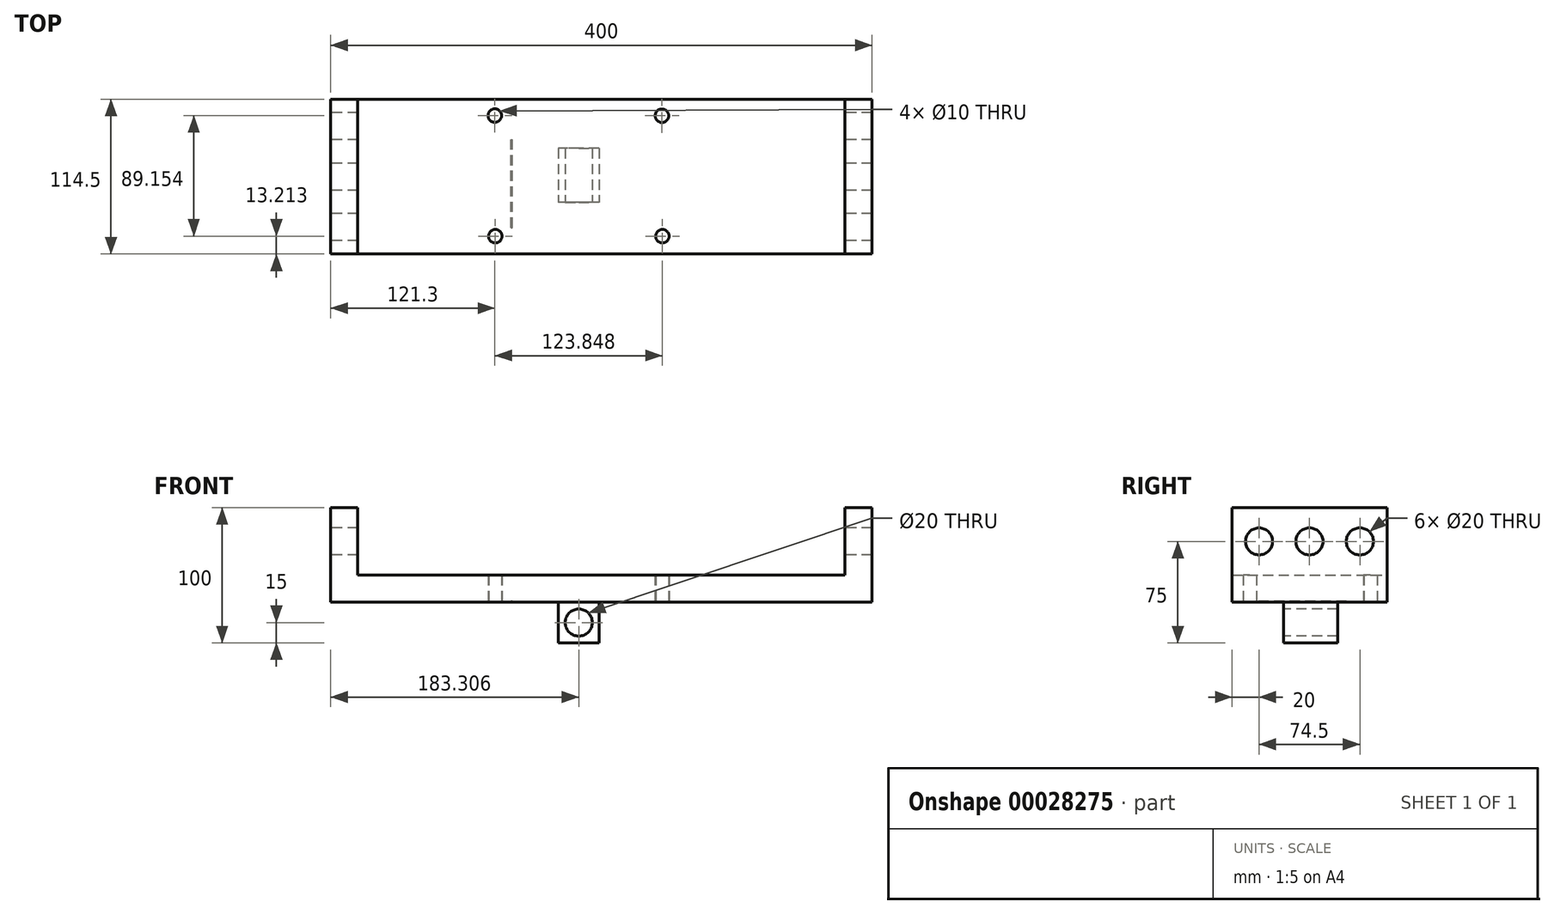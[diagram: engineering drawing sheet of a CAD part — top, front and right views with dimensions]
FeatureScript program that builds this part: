
annotation { "Feature Type Name" : "Feature", "Feature Type Description" : "" }
export const myFeature = defineFeature(function(context is Context, id is Id, definition is map)
    precondition{}
    {
        {
            var Q0;
            Q0=qCreatedBy(makeId("Top.planeOp"),FACE);
            var sketch = newSketch(context, id + "F0", { "sketchPlane" : qUnion([Q0])});
            skLineSegment(sketch, "E0.bottom", {"start": v(0, 0) * mm, "end": v(400, 0) * mm});
            skLineSegment(sketch, "E0.top", {"start": v(0, 114.5) * mm, "end": v(400, 114.5) * mm});
            skLineSegment(sketch, "E0.left", {"start": v(0, 0) * mm, "end": v(0, 114.5) * mm});
            skLineSegment(sketch, "E0.right", {"start": v(400, 0) * mm, "end": v(400, 114.5) * mm});
            skSolve(sketch);
        }
        {
            var Q0;
            Q0=makeQuery(id+"F0.imprint","IMPRINT",FACE,{"disambiguationData":[TD([[makeQuery(id+"F0.imprint","IMPRINT",EDGE,{"derivedFrom":sQuery(id+"F0.wireOp",EDGE,"E0.bottom")}),1.0]])]});
            extrude(context, id + "F1", {"entities" : qUnion([Q0]), "depth" : 20 * mm});
        }
        {
            var Q0;
            Q0=makeQuery(id+"F1.opExtrude","CAP_FACE",FACE,{"disambiguationData":[OSD([sQuery(id+"F0.wireOp",EDGE,"E0.bottom"),sQuery(id+"F0.wireOp",EDGE,"E0.top"),sQuery(id+"F0.wireOp",EDGE,"E0.left"),sQuery(id+"F0.wireOp",EDGE,"E0.right")])],"isStart":false});
            var sketch = newSketch(context, id + "F12", { "sketchPlane" : qUnion([Q0])});
            skLineSegment(sketch, "E1.bottom", {"start": v(0, 0) * mm, "end": v(20, 0) * mm});
            skLineSegment(sketch, "E1.top", {"start": v(0, 114.5) * mm, "end": v(20, 114.5) * mm});
            skLineSegment(sketch, "E1.left", {"start": v(0, 0) * mm, "end": v(0, 114.5) * mm});
            skLineSegment(sketch, "E1.right", {"start": v(20, 0) * mm, "end": v(20, 114.5) * mm});
            skLineSegment(sketch, "E2.bottom", {"start": v(400, 0) * mm, "end": v(380, 0) * mm});
            skLineSegment(sketch, "E2.top", {"start": v(400, 114.5) * mm, "end": v(380, 114.5) * mm});
            skLineSegment(sketch, "E2.left", {"start": v(400, 0) * mm, "end": v(400, 114.5) * mm});
            skLineSegment(sketch, "E2.right", {"start": v(380, 0) * mm, "end": v(380, 114.5) * mm});
            skSolve(sketch);
        }
        {
            var Q0;
            Q0 = qSketchRegion(id + "F12", true);
            extrude(context, id + "F13", {"entities" : qUnion([Q0]), "operationType" : NewBodyOperationType.ADD, "depth" : 50 * mm});
        }
        {
            var Q0;
            Q0=makeQuery(id+"F13.boolean.opBoolean","MERGE",FACE,{"derivedFrom":[makeQuery(id+"F1.opExtrude","SWEPT_FACE",FACE,{"disambiguationData":[OSD([sQuery(id+"F0.wireOp",EDGE,"E0.left")])]}),makeQuery(id+"F13.opExtrude","SWEPT_FACE",FACE,{"disambiguationData":[OSD([sQuery(id+"F12.wireOp",EDGE,"E1.left")])]})]});
            var sketch = newSketch(context, id + "F2", { "sketchPlane" : qUnion([Q0])});
            skLineSegment(sketch, "E3", {"start": v(-114.5, 70) * mm, "end": v(0, 70) * mm});
            skCircle(sketch, "E4", {"center": v(-20, 45) * mm, "radius": 10 * mm});
            skCircle(sketch, "E5", {"center": v(-94.5, 45) * mm, "radius": 10 * mm});
            skCircle(sketch, "E6", {"center": v(-57.25, 45) * mm, "radius": 10 * mm});
            skSolve(sketch);
        }
        {
            var Q0;
            Q0 = qSketchRegion(id + "F2", true);
            var Q1;
            {var subQ0=sQuery(id+"F2.wireOp",EDGE,"f415a451-caa5-4d60-8094-ee07f51d5886");var subQ1=sQuery(id+"F2.wireOp",EDGE,"d71bda7b-f379-47d4-bd46-1eae14bf07e1");var subQ3=makeQuery(id+"F2.imprint","INTERSECT",VERTEX,{"disambiguationData":[OD(0.0)],"derivedFrom":[subQ1,subQ0]});Q1=makeQuery(id+"F2.imprint","IMPRINT",FACE,{"disambiguationData":[TD([[makeQuery(id+"F2.imprint","IMPRINT",EDGE,{"disambiguationData":[TD([[subQ3,-1.0]])],"derivedFrom":subQ1}),1.0]])]});}
            extrude(context, id + "F3", {"entities" : qUnion([Q0, Q1]), "operationType" : NewBodyOperationType.REMOVE, "oppositeDirection" : true, "depth" : 410 * mm});
        }
        {
            var Q0;
            Q0=makeQuery(id+"F1.opExtrude","CAP_FACE",FACE,{"disambiguationData":[OSD([sQuery(id+"F0.wireOp",EDGE,"E0.bottom"),sQuery(id+"F0.wireOp",EDGE,"E0.top"),sQuery(id+"F0.wireOp",EDGE,"E0.left"),sQuery(id+"F0.wireOp",EDGE,"E0.right")])],"isStart":true});
            var sketch = newSketch(context, id + "F14", { "sketchPlane" : qUnion([Q0])});
            skCircle(sketch, "E7", {"center": v(121.3, -102.37) * mm, "radius": 5 * mm});
            skCircle(sketch, "E8", {"center": v(244.76, -102.25) * mm, "radius": 5 * mm});
            skCircle(sketch, "E9.MirrorC", {"center": v(245.15, -13.21) * mm, "radius": 5 * mm});
            skLineSegment(sketch, "E10.MirrorC", {"start": v(221.38, -13.21) * mm, "end": v(221.38, -13.21) * mm});
            skCircle(sketch, "E11.MirrorC", {"center": v(121.65, -13.21) * mm, "radius": 5 * mm});
            skPoint(sketch, "E12.orphan", {"position": v(200, -114.5) * mm});
            skPoint(sketch, "E13.end.orphan", {"position": v(200, 0) * mm});
            skPoint(sketch, "E13.start.orphan", {"position": v(200, -57.25) * mm});
            skLineSegment(sketch, "E14", {"start": v(244.76, -102.25) * mm, "end": v(121.26, -102.25) * mm});
            skLineSegment(sketch, "E15", {"start": v(245.15, -13.21) * mm, "end": v(121.65, -13.21) * mm});
            skLineSegment(sketch, "E16", {"start": v(244.76, -102.25) * mm, "end": v(245.19, -13.21) * mm});
            skLineSegment(sketch, "E17.0", {"start": v(163.78, -101.86) * mm, "end": v(164.21, -12.83) * mm});
            skSolve(sketch);
        }
        {
            var Q0;
            Q0 = qSketchRegion(id + "F14", true);
            extrude(context, id + "F4", {"entities" : qUnion([Q0]), "operationType" : NewBodyOperationType.REMOVE, "oppositeDirection" : true, "depth" : 40 * mm});
        }
        {
            var Q0;
            Q0=makeQuery(id+"F14.imprint","IMPRINT",FACE,{"disambiguationData":[TD([[makeQuery(id+"F14.imprint","IMPRINT",EDGE,{"derivedFrom":sQuery(id+"F14.wireOp",EDGE,"E7")}),-1.0]])]});
            var sketch = newSketch(context, id + "F15", { "sketchPlane" : qUnion([Q0])});
            skLineSegment(sketch, "E18.0", {"start": v(233.01, -102.2) * mm, "end": v(233.44, -13.16) * mm});
            skLineSegment(sketch, "E19.0", {"start": v(232.01, -102.19) * mm, "end": v(232.44, -13.15) * mm});
            skLineSegment(sketch, "E20", {"start": v(233.01, -102.2) * mm, "end": v(232.01, -102.19) * mm});
            skLineSegment(sketch, "E21", {"start": v(121.02, -102.28) * mm, "end": v(121.63, -13.25) * mm});
            skLineSegment(sketch, "E22", {"start": v(121.59, -19.54) * mm, "end": v(133.34, -19.62) * mm});
            skLineSegment(sketch, "E23.bottom", {"start": v(133.34, -19.62) * mm, "end": v(134.34, -19.62) * mm});
            skLineSegment(sketch, "E23.top", {"start": v(133.34, -84.48) * mm, "end": v(134.34, -84.48) * mm});
            skLineSegment(sketch, "E23.left", {"start": v(133.34, -19.62) * mm, "end": v(133.34, -84.48) * mm});
            skLineSegment(sketch, "E23.right", {"start": v(134.34, -19.62) * mm, "end": v(134.34, -84.48) * mm});
            skSolve(sketch);
        }
        {
            var Q0;
            Q0 = qSketchRegion(id + "F15", true);
            extrude(context, id + "F5", {"entities" : qUnion([Q0]), "operationType" : NewBodyOperationType.REMOVE, "oppositeDirection" : true, "depth" : 1 * mm});
        }
        {
            var Q0;
            Q0 = qSketchRegion(id + "F15", true);
            extrude(context, id + "F6", {"entities" : qUnion([Q0]), "operationType" : NewBodyOperationType.REMOVE, "oppositeDirection" : true, "depth" : 1 * mm});
        }
        {
            var Q0;
            Q0=sQuery(id+"F15.wireOp",EDGE,"E18.0");
            var Q1;
            Q1=sQuery(id+"F15.wireOp",EDGE,"E19.0");
            var Q2;
            Q2=sQuery(id+"F15.wireOp",EDGE,"E20");
            extrude(context, id + "F7", {"bodyType" : ToolBodyType.SURFACE, "surfaceEntities" : qUnion([Q0, Q1, Q2]), "oppositeDirection" : true, "depth" : 1 * mm});
        }
        {
            var Q0;
            Q0=makeQuery(id+"F1.opExtrude","CAP_FACE",FACE,{"disambiguationData":[OSD([sQuery(id+"F0.wireOp",EDGE,"E0.bottom"),sQuery(id+"F0.wireOp",EDGE,"E0.top"),sQuery(id+"F0.wireOp",EDGE,"E0.left"),sQuery(id+"F0.wireOp",EDGE,"E0.right")])],"isStart":true});
            var sketch = newSketch(context, id + "F8", { "sketchPlane" : qUnion([Q0])});
            skLineSegment(sketch, "E24.rect.bottom", {"start": v(198.3, -78.08) * mm, "end": v(168.3, -78.08) * mm});
            skLineSegment(sketch, "E24.rect.top", {"start": v(198.3, -38.08) * mm, "end": v(168.3, -38.08) * mm});
            skLineSegment(sketch, "E24.rect.left", {"start": v(198.3, -78.08) * mm, "end": v(198.3, -38.08) * mm});
            skLineSegment(sketch, "E24.rect.right", {"start": v(168.3, -78.08) * mm, "end": v(168.3, -38.08) * mm});
            skPoint(sketch, "E24.rect.middle", {"position": v(183.3, -58.08) * mm});
            skSolve(sketch);
        }
        {
            var Q0;
            Q0 = qSketchRegion(id + "F8", true);
            extrude(context, id + "F9", {"entities" : qUnion([Q0]), "operationType" : NewBodyOperationType.ADD, "depth" : 30 * mm});
        }
        {
            var Q0;
            Q0=makeQuery(id+"F9.opExtrude","SWEPT_FACE",FACE,{"disambiguationData":[OSD([sQuery(id+"F8.wireOp",EDGE,"E24.rect.top")])]});
            var sketch = newSketch(context, id + "F10", { "sketchPlane" : qUnion([Q0])});
            skCircle(sketch, "E25", {"center": v(183.3, -15) * mm, "radius": 10 * mm});
            skSolve(sketch);
        }
        {
            var Q0;
            Q0 = qSketchRegion(id + "F10", true);
            extrude(context, id + "F11", {"entities" : qUnion([Q0]), "operationType" : NewBodyOperationType.REMOVE, "oppositeDirection" : true, "depth" : 51.28 * mm});
        }
    });
